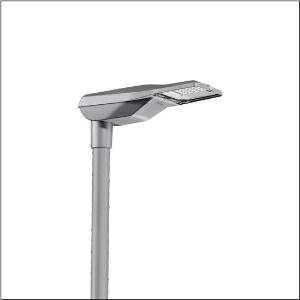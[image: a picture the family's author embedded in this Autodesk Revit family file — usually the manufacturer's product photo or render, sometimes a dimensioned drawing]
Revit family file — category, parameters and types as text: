
# Revit family: streetlight_sl_21_micro___st1_0a_5xe5d43a08cb_bbe5
name_source: partatom
category: Lighting Fixtures
units: mm (PartAtom-declared; Revit-internal decimal feet)

## family parameters
Cut with Voids When Loaded = No
Host = Face
Light Source = No
Part Type = Normal
Room Calculation Point = No
Round Connector Dimension = Use Diameter
Shared = No

## types (1)
- --- (1 x LED, 2380 lm, 15.8 W, 4000K)
    Apparent Load = 16 VA
    CIE Flux Codes = 37 72 97 100 100
    Color Rendering = 70
    Color Temperature = 4000K
    Default Elevation = 1800 mm
    Description = Streetlight SL 21 micro, mast luminaire, primary light control with lens, of PMMA, primary optical cover: cover, of toughened safety glass, transparent, light distribution: ST1.0a, light emission: direct distribution, primary light characteristic: asymmetric, installation type: side-entry, post-top, LED, 3G 1.5mm², High Power LED, rated luminous flux: 2.380lm, luminous efficacy: 151lm/W, light colour: 740, colour temperature: 4000K, control: flexible luminous flux parameterisation, time-dependent luminous flux control, constant luminous flux control, overheat protection, mains connection: 230..240V, AC, 50/60Hz, connection cable pre-assembled, cable length: 5,5m, wiring characteristics: H07RN-F, start of lifetime: 16W, end of service life: 16W, reduction: 9W, luminaire housing, of diecast aluminium, powder-coated, Siteco® metallic grey (DB 702S), corrosivity category C5 mid according to DIN EN ISO 12944, please order mast flange separately, inclination adjustable: 0°, 5°, 10°, 15°, sealing non-destructively replaceable, multi-level sealing system, length: 528mm, width: 235mm, height: 110mm, mast flange for spigot size: 42mm (side-entry): 5XC10008XM4, 60/48mm (side-entry/post-top): 5XC10108XM2, 76/60mm (side-entry/post-top): 5XC10108XM1, protection rating (complete): IP66, insulation class (complete): insulation class II (safety insulation), certification: CE, ENEC, ENEC+, VDE, impact resistance: IK09, permissible operating ambient temperature for outdoor applications: -40..+50°C, standard-compliant lighting for roads and squares, packaging unit: 1 piece

Light Distribution: ST1.0a
    Height = 110 mm
    Lamp = 1 x LED
    Lamp Light Flux = 2380 lm
    Lamp Power = 15.8 W
    Lamp count = 1
    Length = 528 mm
    Luminous efficacy = 151 lm/W
    Manufacturer = Siteco
    ModVariant = No
    Model = 5XE5D43A08CB
    Number of Poles = 1
    OnlyDefault = Yes
    Power Factor = 1
    Product Name = Streetlight SL 21 micro | ST1.0a
    Product group = mast luminaire | pylon top
    ProductGroupID = 6100
    Protection Class = Protection class II
    Protection Degree = IP 66
    RLX_Detail_Level = 1
    RLX_Emergency_Light_Flux = 0 lm
    RLX_Emergency_Type = 0
    RLX_Emergency_Type_DB = No
    RlxData = <blob elided: 97997 chars, md5=d4408c90>
    Socket = socket
    Standby Power = 0 W
    System Light Flux = 2380 lm
    System Power = 16 W
    Type Comments = factory setting: luminous flux: 100 % | Output Level: 100 % | 300 mA
    Type Image = l_1006881.jpg
    URL = http://relux.com
    VarID = @adj_087905
    Voltage = 0 V
    Weight = 0.00 kg
    Width = 235 mm

## geometry (parser evidence)
native form markers: Blend x4, Sweep x9
no freeform markers — native parametric forms only
